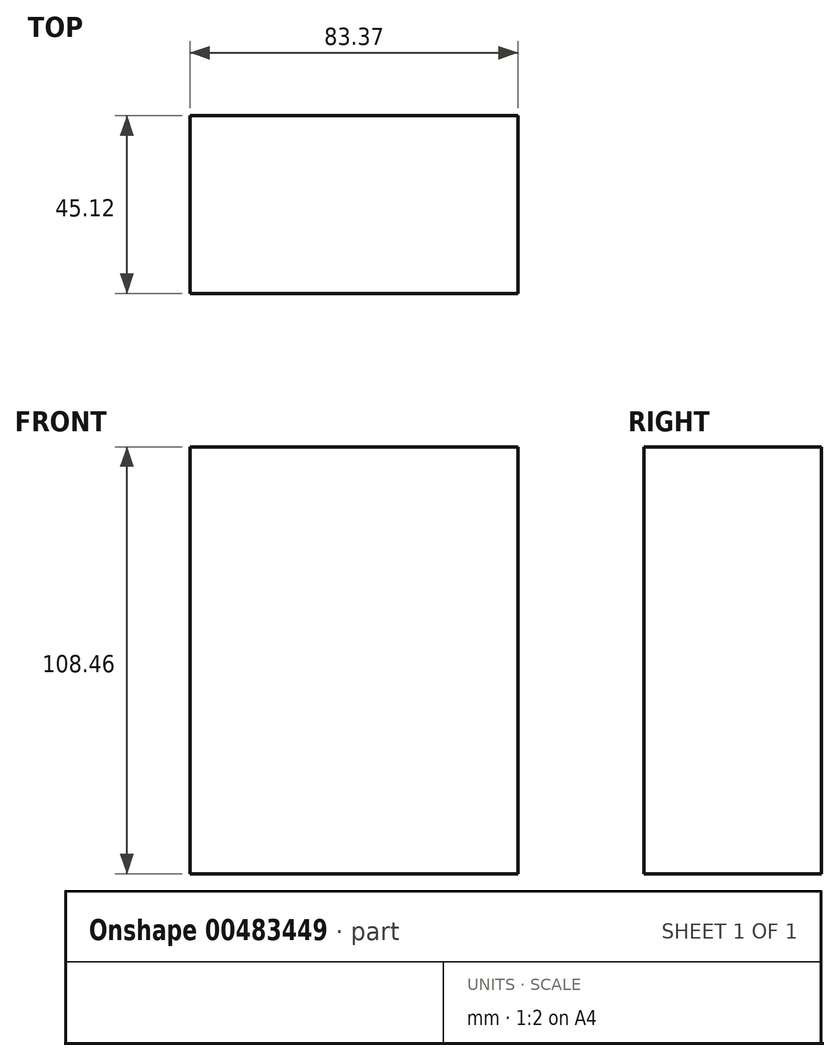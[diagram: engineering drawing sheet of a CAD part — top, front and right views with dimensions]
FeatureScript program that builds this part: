
annotation { "Feature Type Name" : "Feature", "Feature Type Description" : "" }
export const myFeature = defineFeature(function(context is Context, id is Id, definition is map)
    precondition{}
    {
        {
            var Q0;
            Q0=qCreatedBy(makeId("Top.planeOp"),FACE);
            var sketch = newSketch(context, id + "F0", { "sketchPlane" : qUnion([Q0])});
            skLineSegment(sketch, "E0.bottom", {"start": v(0, 1.44) * mm, "end": v(83.37, 1.44) * mm});
            skLineSegment(sketch, "E0.top", {"start": v(0, -43.68) * mm, "end": v(83.37, -43.68) * mm});
            skLineSegment(sketch, "E0.left", {"start": v(0, 1.44) * mm, "end": v(0, -43.68) * mm});
            skLineSegment(sketch, "E0.right", {"start": v(83.37, 1.44) * mm, "end": v(83.37, -43.68) * mm});
            skSolve(sketch);
        }
        {
            var Q0;
            Q0=makeQuery(id+"F0.imprint","IMPRINT",FACE,{"disambiguationData":[TD([[makeQuery(id+"F0.imprint","IMPRINT",EDGE,{"derivedFrom":sQuery(id+"F0.wireOp",EDGE,"E0.bottom")}),-1.0]])]});
            extrude(context, id + "F1", {"entities" : qUnion([Q0]), "depth" : 108.46 * mm, "offsetDistance" : 25.4 * mm});
        }
    });
